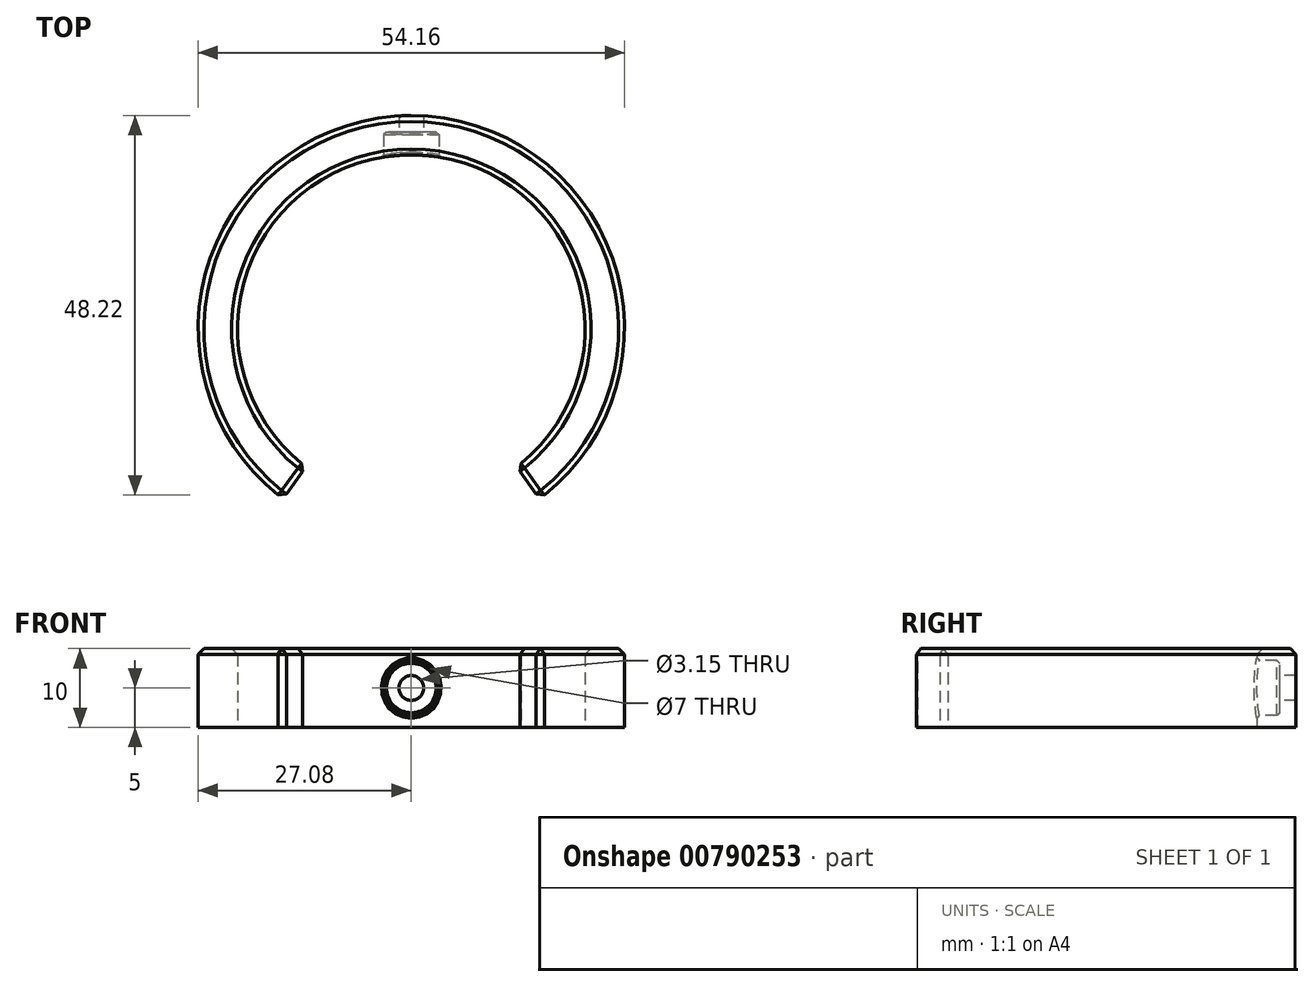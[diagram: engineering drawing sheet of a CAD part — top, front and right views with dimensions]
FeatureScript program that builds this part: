
annotation { "Feature Type Name" : "Feature", "Feature Type Description" : "" }
export const myFeature = defineFeature(function(context is Context, id is Id, definition is map)
    precondition{}
    {
        {
            var Q0;
            Q0=qCreatedBy(makeId("Top.planeOp"),FACE);
            var sketch = newSketch(context, id + "F0", { "sketchPlane" : qUnion([Q0])});
            skArc(sketch, "E0", {"start": v(0, 22.07) * mm, "mid": v(-22.07, 0) * mm, "end": v(0, -22.07) * mm});
            skArc(sketch, "E1.0", {"start": v(0, 27.08) * mm, "mid": v(-27.08, 0) * mm, "end": v(0, -27.08) * mm});
            skLineSegment(sketch, "E2", {"start": v(0, -27.08) * mm, "end": v(0, 27.08) * mm});
            skLineSegment(sketch, "E3", {"start": v(-13.37, -17.56) * mm, "end": v(-16.3, -21.62) * mm});
            skArc(sketch, "E4.MirrorCS", {"start": v(0, 22.07) * mm, "mid": v(22.07, 0) * mm, "end": v(0, -22.07) * mm});
            skArc(sketch, "E5.MirrorCS", {"start": v(0, 27.08) * mm, "mid": v(27.08, 0) * mm, "end": v(0, -27.08) * mm});
            skLineSegment(sketch, "E6.MirrorCS", {"start": v(13.37, -17.56) * mm, "end": v(16.3, -21.62) * mm});
            skSolve(sketch);
        }
        {
            var Q0;
            {var subQ3=sQuery(id+"F0.wireOp",EDGE,"E3");Q0=makeQuery(id+"F0.imprint","IMPRINT",FACE,{"disambiguationData":[TD([[makeQuery(id+"F0.imprint","IMPRINT",EDGE,{"derivedFrom":subQ3}),-1.0]])]});}
            var Q1;
            {var subQ3=sQuery(id+"F0.wireOp",EDGE,"E6.MirrorCS");Q1=makeQuery(id+"F0.imprint","IMPRINT",FACE,{"disambiguationData":[TD([[makeQuery(id+"F0.imprint","IMPRINT",EDGE,{"derivedFrom":subQ3}),1.0]])]});}
            extrude(context, id + "F1", {"entities" : qUnion([Q0, Q1]), "depth" : 10 * mm, "offsetDistance" : 25 * mm});
        }
        {
            var Q0;
            Q0=makeQuery(id+"F1.opExtrude","SWEPT_EDGE",EDGE,{"disambiguationData":[OSD([sQuery(id+"F0.wireOp",EDGE,"E4.MirrorCS"),sQuery(id+"F0.wireOp",EDGE,"E6.MirrorCS")])]});
            var Q1;
            Q1=makeQuery(id+"F1.opExtrude","SWEPT_EDGE",EDGE,{"disambiguationData":[OSD([sQuery(id+"F0.wireOp",EDGE,"E0"),sQuery(id+"F0.wireOp",EDGE,"E3")])]});
            var Q2;
            Q2=makeQuery(id+"F1.opExtrude","SWEPT_EDGE",EDGE,{"disambiguationData":[OSD([sQuery(id+"F0.wireOp",EDGE,"E5.MirrorCS"),sQuery(id+"F0.wireOp",EDGE,"E6.MirrorCS")])]});
            var Q3;
            Q3=makeQuery(id+"F1.opExtrude","SWEPT_EDGE",EDGE,{"disambiguationData":[OSD([sQuery(id+"F0.wireOp",EDGE,"E1.0"),sQuery(id+"F0.wireOp",EDGE,"E3")])]});
            var Q4;
            Q4=makeQuery(id+"F1.opExtrude","CAP_EDGE",EDGE,{"disambiguationData":[OSD([sQuery(id+"F0.wireOp",EDGE,"E1.0"),sQuery(id+"F0.wireOp",EDGE,"E5.MirrorCS")])],"isStart":false});
            var Q5;
            Q5=makeQuery(id+"F1.opExtrude","CAP_EDGE",EDGE,{"disambiguationData":[OSD([sQuery(id+"F0.wireOp",EDGE,"E0"),sQuery(id+"F0.wireOp",EDGE,"E4.MirrorCS")])],"isStart":false});
            var Q6;
            Q6=makeQuery(id+"F1.opExtrude","CAP_EDGE",EDGE,{"disambiguationData":[OSD([sQuery(id+"F0.wireOp",EDGE,"E3")])],"isStart":false});
            var Q7;
            Q7=makeQuery(id+"F1.opExtrude","CAP_EDGE",EDGE,{"disambiguationData":[OSD([sQuery(id+"F0.wireOp",EDGE,"E6.MirrorCS")])],"isStart":false});
            chamfer(context, id + "F2", {"entities" : qUnion([Q0, Q1, Q2, Q3, Q4, Q5, Q6, Q7]), "width" : .75 * mm, "tangentPropagation" : true});
        }
        {
            var Q0;
            Q0=qCreatedBy(makeId("Front.planeOp"),FACE);
            var sketch = newSketch(context, id + "F3", { "sketchPlane" : qUnion([Q0])});
            skLineSegment(sketch, "E7", {"start": v(0, 0) * mm, "end": v(0, 10) * mm});
            skCircle(sketch, "E8", {"center": v(0, 5) * mm, "radius": 1.57 * mm});
            skCircle(sketch, "E9", {"center": v(0, 5) * mm, "radius": 3.5 * mm});
            skSolve(sketch);
        }
        {
            var Q0;
            {var subQ0=sQuery(id+"F3.wireOp",EDGE,"E8");var subQ1=sQuery(id+"F3.wireOp",EDGE,"E7");var subQ2=makeQuery(id+"F3.imprint","INTERSECT",VERTEX,{"disambiguationData":[OD(0.0)],"derivedFrom":[subQ1,subQ0]});Q0=makeQuery(id+"F3.imprint","IMPRINT",FACE,{"disambiguationData":[TD([[makeQuery(id+"F3.imprint","IMPRINT",EDGE,{"disambiguationData":[TD([[subQ2,-1.0]])],"derivedFrom":subQ1}),1.0]])]});}
            var Q1;
            {var subQ0=sQuery(id+"F3.wireOp",EDGE,"E8");var subQ1=sQuery(id+"F3.wireOp",EDGE,"E7");var subQ2=makeQuery(id+"F3.imprint","INTERSECT",VERTEX,{"disambiguationData":[OD(0.0)],"derivedFrom":[subQ1,subQ0]});Q1=makeQuery(id+"F3.imprint","IMPRINT",FACE,{"disambiguationData":[TD([[makeQuery(id+"F3.imprint","IMPRINT",EDGE,{"disambiguationData":[TD([[subQ2,-1.0]])],"derivedFrom":subQ1}),-1.0]])]});}
            extrude(context, id + "F4", {"entities" : qUnion([Q0, Q1]), "operationType" : NewBodyOperationType.REMOVE, "oppositeDirection" : true, "depth" : 30.99 * mm, "offsetDistance" : 25 * mm});
        }
        {
            var Q0;
            {var subQ0=sQuery(id+"F3.wireOp",EDGE,"E9");var subQ1=sQuery(id+"F3.wireOp",EDGE,"E7");var subQ2=makeQuery(id+"F3.imprint","INTERSECT",VERTEX,{"disambiguationData":[OD(0.0)],"derivedFrom":[subQ1,subQ0]});Q0=makeQuery(id+"F3.imprint","IMPRINT",FACE,{"disambiguationData":[TD([[makeQuery(id+"F3.imprint","IMPRINT",EDGE,{"disambiguationData":[TD([[subQ2,-1.0]])],"derivedFrom":subQ1}),1.0]])]});}
            var Q1;
            {var subQ0=sQuery(id+"F3.wireOp",EDGE,"E9");var subQ1=sQuery(id+"F3.wireOp",EDGE,"E7");var subQ2=makeQuery(id+"F3.imprint","INTERSECT",VERTEX,{"disambiguationData":[OD(0.0)],"derivedFrom":[subQ1,subQ0]});Q1=makeQuery(id+"F3.imprint","IMPRINT",FACE,{"disambiguationData":[TD([[makeQuery(id+"F3.imprint","IMPRINT",EDGE,{"disambiguationData":[TD([[subQ2,-1.0]])],"derivedFrom":subQ1}),-1.0]])]});}
            extrude(context, id + "F5", {"entities" : qUnion([Q0, Q1]), "operationType" : NewBodyOperationType.REMOVE, "oppositeDirection" : true, "depth" : 25 * mm, "offsetDistance" : 25 * mm});
        }
        {
            var Q0;
            Q0=makeQuery(id+"F5.boolean.opBoolean","INTERSECT",EDGE,{"derivedFrom":[makeQuery(id+"F1.opExtrude","SWEPT_FACE",FACE,{"disambiguationData":[OSD([sQuery(id+"F0.wireOp",EDGE,"E0"),sQuery(id+"F0.wireOp",EDGE,"E4.MirrorCS")])]}),makeQuery(id+"F5.opExtrude","SWEPT_FACE",FACE,{"disambiguationData":[OSD([sQuery(id+"F3.wireOp",EDGE,"E9")])]})]});
            var Q1;
            Q1=makeQuery(id+"F5.boolean.opBoolean","COPY",EDGE,{"derivedFrom":makeQuery(id+"F5.opExtrude","CAP_EDGE",EDGE,{"disambiguationData":[OSD([sQuery(id+"F3.wireOp",EDGE,"E9")])],"isStart":false})});
            var Q2;
            Q2=makeQuery(id+"F5.boolean.opBoolean","COPY",EDGE,{"derivedFrom":makeQuery(id+"F5.opExtrude","CAP_EDGE",EDGE,{"disambiguationData":[OSD([sQuery(id+"F3.wireOp",EDGE,"E8")])],"isStart":false})});
            chamfer(context, id + "F6", {"entities" : qUnion([Q0, Q1, Q2]), "width" : .35 * mm, "tangentPropagation" : true});
        }
    });
